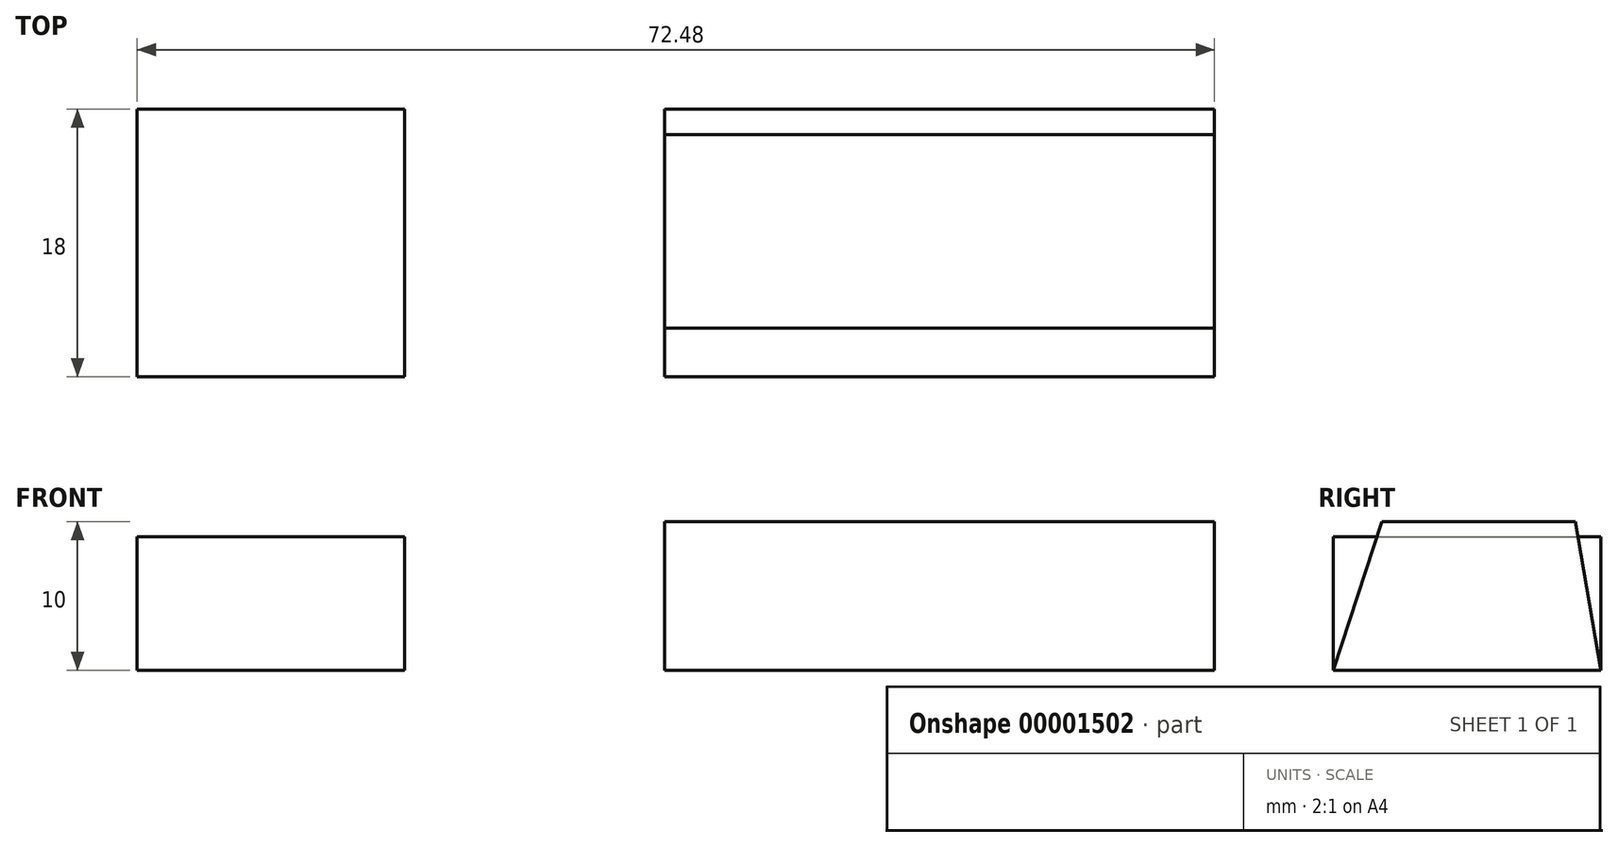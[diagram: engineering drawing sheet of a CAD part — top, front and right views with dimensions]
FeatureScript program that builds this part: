
annotation { "Feature Type Name" : "Feature", "Feature Type Description" : "" }
export const myFeature = defineFeature(function(context is Context, id is Id, definition is map)
    precondition{}
    {
        {
            var Q0;
            Q0=qCreatedBy(makeId("Top.planeOp"),FACE);
            var sketch = newSketch(context, id + "F0", { "sketchPlane" : qUnion([Q0])});
            skLineSegment(sketch, "E0.bottom", {"start": v(0, 0) * mm, "end": v(37, 0) * mm});
            skLineSegment(sketch, "E0.top", {"start": v(0, 18) * mm, "end": v(37, 18) * mm});
            skLineSegment(sketch, "E0.left", {"start": v(0, 0) * mm, "end": v(0, 18) * mm});
            skLineSegment(sketch, "E0.right", {"start": v(37, 0) * mm, "end": v(37, 18) * mm});
            skSolve(sketch);
        }
        {
            var Q0;
            Q0=makeQuery(id+"F0.imprint","IMPRINT",FACE,{"disambiguationData":[TD([[makeQuery(id+"F0.imprint","IMPRINT",EDGE,{"derivedFrom":sQuery(id+"F0.wireOp",EDGE,"E0.bottom")}),1.0]])]});
            extrude(context, id + "F1", {"entities" : qUnion([Q0]), "depth" : 10 * mm});
        }
        {
            var Q0;
            Q0=makeQuery(id+"F1.opExtrude","SWEPT_FACE",FACE,{"disambiguationData":[OSD([sQuery(id+"F0.wireOp",EDGE,"E0.right")])]});
            var sketch = newSketch(context, id + "F2", { "sketchPlane" : qUnion([Q0])});
            skLineSegment(sketch, "E1", {"start": v(0, 0) * mm, "end": v(3.27, 10) * mm});
            skLineSegment(sketch, "E2", {"start": v(3.27, 10) * mm, "end": v(16.3, 10) * mm});
            skLineSegment(sketch, "E3", {"start": v(16.3, 10) * mm, "end": v(18, 0) * mm});
            skLineSegment(sketch, "E4", {"start": v(18, 0) * mm, "end": v(0, 0) * mm});
            skSolve(sketch);
        }
        {
            var Q0;
            {var subQ2=sQuery(id+"F2.wireOp",EDGE,"E1");Q0=makeQuery(id+"F2.imprint","IMPRINT",FACE,{"disambiguationData":[TD([[makeQuery(id+"F2.imprint","IMPRINT",EDGE,{"derivedFrom":subQ2}),1.0]])]});}
            var Q1;
            {var subQ2=sQuery(id+"F2.wireOp",EDGE,"E3");Q1=makeQuery(id+"F2.imprint","IMPRINT",FACE,{"disambiguationData":[TD([[makeQuery(id+"F2.imprint","IMPRINT",EDGE,{"derivedFrom":subQ2}),1.0]])]});}
            extrude(context, id + "F3", {"entities" : qUnion([Q0, Q1]), "operationType" : NewBodyOperationType.REMOVE, "oppositeDirection" : true, "depth" : 50.62 * mm});
        }
        {
            var Q0;
            Q0=qCreatedBy(makeId("Top.planeOp"),FACE);
            var sketch = newSketch(context, id + "F4", { "sketchPlane" : qUnion([Q0])});
            skLineSegment(sketch, "E5.bottom", {"start": v(-17.48, 0) * mm, "end": v(-35.48, 0) * mm});
            skLineSegment(sketch, "E5.top", {"start": v(-17.48, 18) * mm, "end": v(-35.48, 18) * mm});
            skLineSegment(sketch, "E5.left", {"start": v(-17.48, 0) * mm, "end": v(-17.48, 18) * mm});
            skLineSegment(sketch, "E5.right", {"start": v(-35.48, 0) * mm, "end": v(-35.48, 18) * mm});
            skSolve(sketch);
        }
        {
            var Q0;
            Q0 = qSketchRegion(id + "F4", true);
            extrude(context, id + "F5", {"entities" : qUnion([Q0]), "depth" : 9 * mm});
        }
    });
